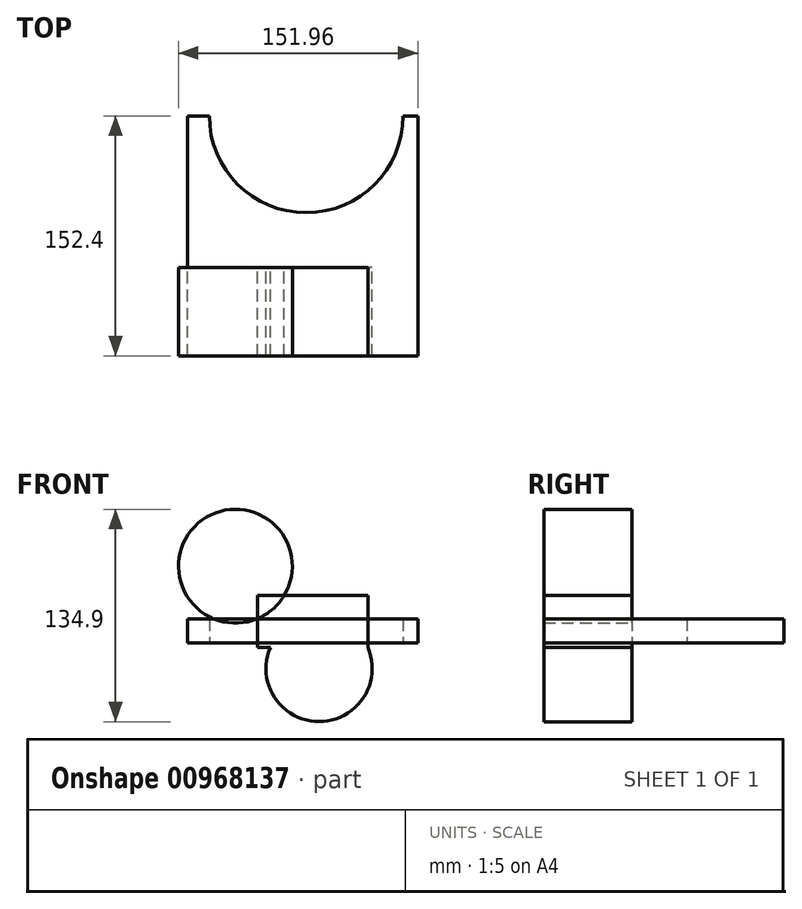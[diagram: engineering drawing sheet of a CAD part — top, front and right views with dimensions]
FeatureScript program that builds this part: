
annotation { "Feature Type Name" : "Feature", "Feature Type Description" : "" }
export const myFeature = defineFeature(function(context is Context, id is Id, definition is map)
    precondition{}
    {
        {
            var Q0;
            Q0=qCreatedBy(makeId("Top.planeOp"),FACE);
            var sketch = newSketch(context, id + "F0", { "sketchPlane" : qUnion([Q0])});
            skLineSegment(sketch, "E0.bottom", {"start": v(70.87, -56.17) * mm, "end": v(-75.49, -56.17) * mm});
            skLineSegment(sketch, "E0.top", {"start": v(70.87, 96.23) * mm, "end": v(-75.49, 96.23) * mm});
            skLineSegment(sketch, "E0.left", {"start": v(70.87, -56.17) * mm, "end": v(70.87, 96.23) * mm});
            skLineSegment(sketch, "E0.right", {"start": v(-75.49, -56.17) * mm, "end": v(-75.49, 96.23) * mm});
            skCircle(sketch, "E1", {"center": v(0, 96.23) * mm, "radius": 61.52 * mm});
            skSolve(sketch);
        }
        {
            var Q0;
            Q0=makeQuery(id+"F0.imprint","IMPRINT",FACE,{"disambiguationData":[TD([[makeQuery(id+"F0.imprint","IMPRINT",EDGE,{"derivedFrom":sQuery(id+"F0.wireOp",EDGE,"E0.bottom")}),-1.0]])]});
            var Q1;
            {var subQ0=sQuery(id+"F0.wireOp",EDGE,"E1");var subQ1=sQuery(id+"F0.wireOp",EDGE,"E0.top");var subQ2=makeQuery(id+"F0.imprint","INTERSECT",VERTEX,{"disambiguationData":[OD(0.0)],"derivedFrom":[subQ1,subQ0]});Q1=makeQuery(id+"F0.imprint","IMPRINT",FACE,{"disambiguationData":[TD([[makeQuery(id+"F0.imprint","IMPRINT",EDGE,{"disambiguationData":[TD([[subQ2,-1.0]])],"derivedFrom":subQ1}),-1.0]])]});}
            var Q2;
            {var subQ0=sQuery(id+"F0.wireOp",EDGE,"E1");var subQ1=sQuery(id+"F0.wireOp",EDGE,"E0.top");var subQ2=makeQuery(id+"F0.imprint","INTERSECT",VERTEX,{"disambiguationData":[OD(0.0)],"derivedFrom":[subQ1,subQ0]});Q2=makeQuery(id+"F0.imprint","IMPRINT",FACE,{"disambiguationData":[TD([[makeQuery(id+"F0.imprint","IMPRINT",EDGE,{"disambiguationData":[TD([[subQ2,-1.0]])],"derivedFrom":subQ1}),1.0]])]});}
            extrude(context, id + "F1", {"entities" : qUnion([Q0, Q1, Q2]), "depth" : 15 * mm, "offsetDistance" : 25.4 * mm});
        }
        {
            var Q0;
            Q0=qCreatedBy(makeId("Front.planeOp"),FACE);
            var sketch = newSketch(context, id + "F2", { "sketchPlane" : qUnion([Q0])});
            skCircle(sketch, "E2", {"center": v(-44.94, 48.58) * mm, "radius": 36.15 * mm});
            skCircle(sketch, "E3", {"center": v(8.2, -16.44) * mm, "radius": 33.73 * mm});
            skLineSegment(sketch, "E4.bottom", {"start": v(-30.84, 29.87) * mm, "end": v(39.18, 29.87) * mm});
            skLineSegment(sketch, "E4.top", {"start": v(-30.84, -3.09) * mm, "end": v(39.18, -3.09) * mm});
            skLineSegment(sketch, "E4.left", {"start": v(-30.84, 29.87) * mm, "end": v(-30.84, -3.09) * mm});
            skLineSegment(sketch, "E4.right", {"start": v(39.18, 29.87) * mm, "end": v(39.18, -3.09) * mm});
            skLineSegment(sketch, "E5.bottom", {"start": v(-30.84, 29.87) * mm, "end": v(-10.85, 29.87) * mm});
            skLineSegment(sketch, "E5.top", {"start": v(-30.84, 11.4) * mm, "end": v(-10.85, 11.4) * mm});
            skLineSegment(sketch, "E5.left", {"start": v(-30.84, 29.87) * mm, "end": v(-30.84, 11.4) * mm});
            skLineSegment(sketch, "E5.right", {"start": v(-10.85, 29.87) * mm, "end": v(-10.85, 11.4) * mm});
            skSolve(sketch);
        }
        {
            var Q0;
            {var subQ0=sQuery(id+"F2.wireOp",EDGE,"E4.bottom");var subQ1=sQuery(id+"F2.wireOp",EDGE,"E2");var subQ2=makeQuery(id+"F2.imprint","INTERSECT",VERTEX,{"derivedFrom":[subQ1,subQ0]});Q0=makeQuery(id+"F2.imprint","IMPRINT",FACE,{"disambiguationData":[TD([[makeQuery(id+"F2.imprint","IMPRINT",EDGE,{"disambiguationData":[TD([[subQ2,-1.0]])],"derivedFrom":subQ1}),1.0]])]});}
            var Q1;
            {var subQ0=sQuery(id+"F2.wireOp",EDGE,"E5.top");Q1=makeQuery(id+"F2.imprint","IMPRINT",FACE,{"disambiguationData":[TD([[makeQuery(id+"F2.imprint","IMPRINT",EDGE,{"derivedFrom":subQ0}),1.0]])]});}
            var Q2;
            {var subQ0=sQuery(id+"F2.wireOp",EDGE,"E4.right");Q2=makeQuery(id+"F2.imprint","IMPRINT",FACE,{"disambiguationData":[TD([[makeQuery(id+"F2.imprint","IMPRINT",EDGE,{"derivedFrom":subQ0}),-1.0]])]});}
            var Q3;
            {var subQ3=sQuery(id+"F2.wireOp",EDGE,"E5.top");Q3=makeQuery(id+"F2.imprint","IMPRINT",FACE,{"disambiguationData":[TD([[makeQuery(id+"F2.imprint","IMPRINT",EDGE,{"derivedFrom":subQ3}),-1.0]])]});}
            var Q4;
            {var subQ0=sQuery(id+"F2.wireOp",EDGE,"E4.top");var subQ1=sQuery(id+"F2.wireOp",EDGE,"E3");var subQ4=makeQuery(id+"F2.imprint","INTERSECT",VERTEX,{"derivedFrom":[subQ1,subQ0]});Q4=makeQuery(id+"F2.imprint","IMPRINT",FACE,{"disambiguationData":[TD([[makeQuery(id+"F2.imprint","IMPRINT",EDGE,{"disambiguationData":[TD([[subQ4,1.0]])],"derivedFrom":subQ1}),1.0]])]});}
            var Q5;
            {var subQ0=sQuery(id+"F2.wireOp",EDGE,"E4.top");var subQ1=sQuery(id+"F2.wireOp",EDGE,"E3");var subQ2=makeQuery(id+"F2.imprint","INTERSECT",VERTEX,{"derivedFrom":[subQ1,subQ0]});Q5=makeQuery(id+"F2.imprint","IMPRINT",FACE,{"disambiguationData":[TD([[makeQuery(id+"F2.imprint","IMPRINT",EDGE,{"disambiguationData":[TD([[subQ2,-1.0]])],"derivedFrom":subQ1}),1.0]])]});}
            var Q6;
            Q6=makeQuery(id+"F1.opExtrude","SWEPT_FACE",FACE,{"disambiguationData":[OSD([sQuery(id+"F0.wireOp",EDGE,"E0.bottom")])]});
            extrude(context, id + "F3", {"entities" : qUnion([Q0, Q1, Q2, Q3, Q4, Q5]), "endBound" : BoundingType.UP_TO_SURFACE, "depth" : 25.4 * mm, "endBoundEntityFace" : qUnion([Q6]), "offsetDistance" : 25.4 * mm});
        }
    });
